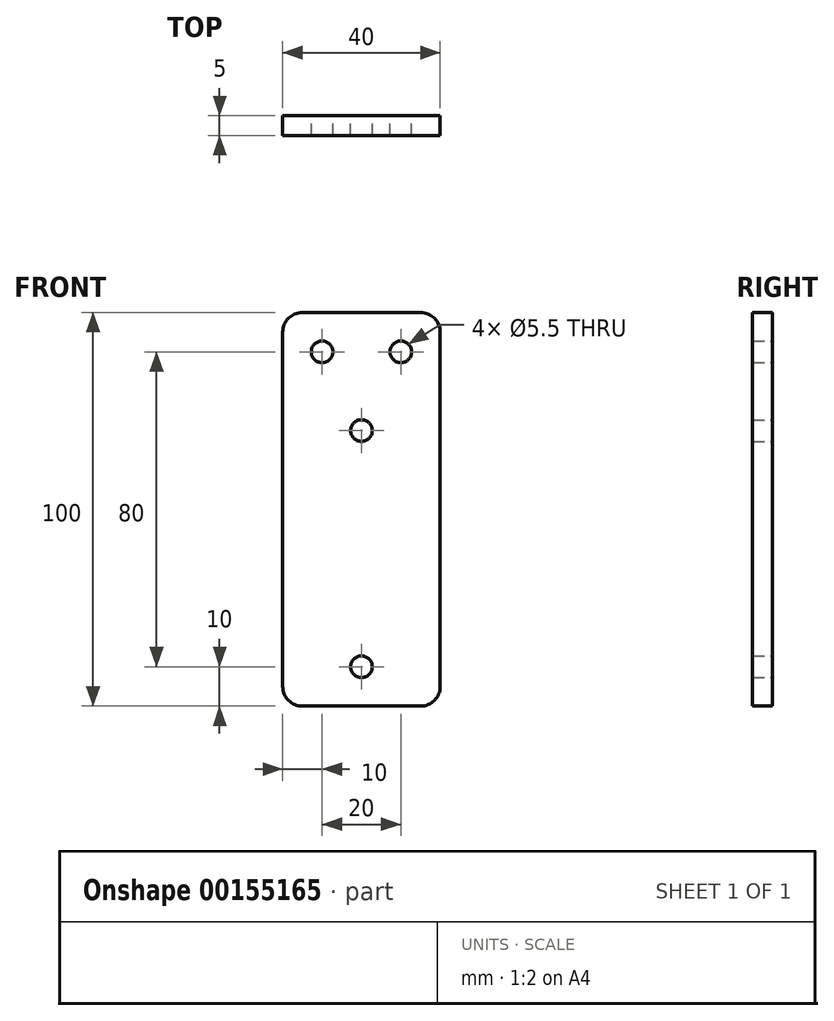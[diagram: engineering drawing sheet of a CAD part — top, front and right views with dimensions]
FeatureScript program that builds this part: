
annotation { "Feature Type Name" : "Feature", "Feature Type Description" : "" }
export const myFeature = defineFeature(function(context is Context, id is Id, definition is map)
    precondition{}
    {
        {
            var Q0;
            Q0=qCreatedBy(makeId("Front.planeOp"),FACE);
            var sketch = newSketch(context, id + "F0", { "sketchPlane" : qUnion([Q0])});
            skLineSegment(sketch, "E0.bottom", {"start": v(0, 0) * mm, "end": v(40, 0) * mm});
            skLineSegment(sketch, "E0.top", {"start": v(0, 100) * mm, "end": v(40, 100) * mm});
            skLineSegment(sketch, "E0.left", {"start": v(0, 0) * mm, "end": v(0, 100) * mm});
            skLineSegment(sketch, "E0.right", {"start": v(40, 0) * mm, "end": v(40, 100) * mm});
            skSolve(sketch);
        }
        {
            var Q0;
            Q0=makeQuery(id+"F0.imprint","IMPRINT",FACE,{"disambiguationData":[TD([[makeQuery(id+"F0.imprint","IMPRINT",EDGE,{"derivedFrom":sQuery(id+"F0.wireOp",EDGE,"E0.bottom")}),1.0]])]});
            extrude(context, id + "F1", {"entities" : qUnion([Q0]), "depth" : 5 * mm});
        }
        {
            var Q0;
            Q0=makeQuery(id+"F1.opExtrude","SWEPT_EDGE",EDGE,{"disambiguationData":[OSD([sQuery(id+"F0.wireOp",EDGE,"E0.top"),sQuery(id+"F0.wireOp",EDGE,"E0.left")])]});
            var Q1;
            Q1=makeQuery(id+"F1.opExtrude","SWEPT_EDGE",EDGE,{"disambiguationData":[OSD([sQuery(id+"F0.wireOp",EDGE,"E0.top"),sQuery(id+"F0.wireOp",EDGE,"E0.right")])]});
            var Q2;
            Q2=makeQuery(id+"F1.opExtrude","SWEPT_EDGE",EDGE,{"disambiguationData":[OSD([sQuery(id+"F0.wireOp",EDGE,"E0.bottom"),sQuery(id+"F0.wireOp",EDGE,"E0.right")])]});
            var Q3;
            Q3=makeQuery(id+"F1.opExtrude","SWEPT_EDGE",EDGE,{"disambiguationData":[OSD([sQuery(id+"F0.wireOp",EDGE,"E0.bottom"),sQuery(id+"F0.wireOp",EDGE,"E0.left")])]});
            fillet(context, id + "F2", {"entities" : qUnion([Q0, Q1, Q2, Q3]), "radius" : 5 * mm, "tangentPropagation" : true, "allowEdgeOverflow" : false});
        }
        {
            var Q0;
            Q0=qCreatedBy(makeId("Front.planeOp"),FACE);
            var sketch = newSketch(context, id + "F3", { "sketchPlane" : qUnion([Q0])});
            skCircle(sketch, "E1", {"center": v(20, 10) * mm, "radius": 2.75 * mm});
            skSolve(sketch);
        }
        {
            var Q0;
            Q0=makeQuery(id+"F3.imprint","IMPRINT",FACE,{"disambiguationData":[TD([[makeQuery(id+"F3.imprint","IMPRINT",EDGE,{"derivedFrom":sQuery(id+"F3.wireOp",EDGE,"E1")}),1.0]])]});
            extrude(context, id + "F4", {"entities" : qUnion([Q0]), "endBound" : BoundingType.THROUGH_ALL, "depth" : 25 * mm});
        }
        {
            var Q0;
            Q0=makeQuery(id+"F4.opExtrude","SWEPT_BODY",BODY,{"disambiguationData":[OSD([sQuery(id+"F3.wireOp",EDGE,"E1")])]});
            var Q1;
            Q1=makeQuery(id+"F1.opExtrude","SWEPT_BODY",BODY,{"disambiguationData":[OSD([sQuery(id+"F0.wireOp",EDGE,"E0.bottom"),sQuery(id+"F0.wireOp",EDGE,"E0.top"),sQuery(id+"F0.wireOp",EDGE,"E0.left"),sQuery(id+"F0.wireOp",EDGE,"E0.right")])]});
            booleanBodies(context, id + "F5", {"operationType" : BooleanOperationType.SUBTRACTION, "tools" : qUnion([Q0]), "targets" : qUnion([Q1]), "keepTools" : true});
        }
        {
            var Q0;
            Q0=makeQuery(id+"F4.opExtrude","SWEPT_BODY",BODY,{"disambiguationData":[OSD([sQuery(id+"F3.wireOp",EDGE,"E1")])]});
            transform(context, id + "F6", {"entities" : qUnion([Q0]), "transformType" : TransformType.TRANSLATION_3D, "dx" : 0 * mm, "dy" : 0 * mm, "dz" : 60 * mm, "makeCopy" : true});
        }
        {
            var Q0;
            Q0=makeQuery(id+"F6.opPattern","COPY",BODY,{"derivedFrom":makeQuery(id+"F4.opExtrude","SWEPT_BODY",BODY,{"disambiguationData":[OSD([sQuery(id+"F3.wireOp",EDGE,"E1")])]}),"instanceName":"1"});
            transform(context, id + "F7", {"entities" : qUnion([Q0]), "transformType" : TransformType.TRANSLATION_3D, "dx" : 10 * mm, "dy" : 0 * mm, "dz" : 20 * mm, "makeCopy" : true});
        }
        {
            var Q0;
            Q0=makeQuery(id+"F6.opPattern","COPY",BODY,{"derivedFrom":makeQuery(id+"F4.opExtrude","SWEPT_BODY",BODY,{"disambiguationData":[OSD([sQuery(id+"F3.wireOp",EDGE,"E1")])]}),"instanceName":"1"});
            transform(context, id + "F8", {"entities" : qUnion([Q0]), "transformType" : TransformType.TRANSLATION_3D, "dx" : -10 * mm, "dy" : 0 * mm, "dz" : 20 * mm, "makeCopy" : true});
        }
        {
            var Q0;
            Q0=makeQuery(id+"F8.opPattern","COPY",BODY,{"derivedFrom":makeQuery(id+"F6.opPattern","COPY",BODY,{"derivedFrom":makeQuery(id+"F4.opExtrude","SWEPT_BODY",BODY,{"disambiguationData":[OSD([sQuery(id+"F3.wireOp",EDGE,"E1")])]}),"instanceName":"1"}),"instanceName":"1"});
            var Q1;
            Q1=makeQuery(id+"F7.opPattern","COPY",BODY,{"derivedFrom":makeQuery(id+"F6.opPattern","COPY",BODY,{"derivedFrom":makeQuery(id+"F4.opExtrude","SWEPT_BODY",BODY,{"disambiguationData":[OSD([sQuery(id+"F3.wireOp",EDGE,"E1")])]}),"instanceName":"1"}),"instanceName":"1"});
            var Q2;
            Q2=makeQuery(id+"F6.opPattern","COPY",BODY,{"derivedFrom":makeQuery(id+"F4.opExtrude","SWEPT_BODY",BODY,{"disambiguationData":[OSD([sQuery(id+"F3.wireOp",EDGE,"E1")])]}),"instanceName":"1"});
            var Q3;
            Q3=makeQuery(id+"F4.opExtrude","SWEPT_BODY",BODY,{"disambiguationData":[OSD([sQuery(id+"F3.wireOp",EDGE,"E1")])]});
            var Q4;
            Q4=makeQuery(id+"F1.opExtrude","SWEPT_BODY",BODY,{"disambiguationData":[OSD([sQuery(id+"F0.wireOp",EDGE,"E0.bottom"),sQuery(id+"F0.wireOp",EDGE,"E0.top"),sQuery(id+"F0.wireOp",EDGE,"E0.left"),sQuery(id+"F0.wireOp",EDGE,"E0.right")])]});
            booleanBodies(context, id + "F9", {"operationType" : BooleanOperationType.SUBTRACTION, "tools" : qUnion([Q0, Q1, Q2, Q3]), "targets" : qUnion([Q4])});
        }
    });
